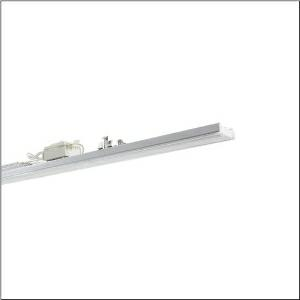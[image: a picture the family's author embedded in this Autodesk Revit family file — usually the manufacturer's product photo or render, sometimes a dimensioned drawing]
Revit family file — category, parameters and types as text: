
# Revit family: licross_r__21_recessed_mo_52te1e7n485g_828a
name_source: partatom
category: Lighting Fixtures
units: mm (PartAtom-declared; Revit-internal decimal feet)

## family parameters
Cut with Voids When Loaded = No
Host = Face
Light Source = No
Part Type = Normal
Room Calculation Point = No
Round Connector Dimension = Use Diameter
Shared = No

## types (1)
- Licross® 21 Recessed MO (1 x LED, 8530 lm, 47.9 W, 4000K)
    Apparent Load = 48 VA
    CIE Flux Codes = 85 95 99 100 100
    Color Rendering = 80
    Color Temperature = 4000K
    Default Elevation = 1800 mm
    Description = Licross® 21 Recessed MO, luminaire insert, of sheet steel, galvanised, coil coated, white, length: 1.500mm, width: 66mm, height: 67mm, LED rated luminous flux: 8.530lm, light colour: 840, control gear: ON/OFF, with plug, 3-pole, with phase selection, mains connection: 220..240V, AC, 50/60Hz, rated input power: 48W, internal wiring halogen-free, primary light control with lens, of plastic, primary optical cover: cover, of PMMA, light emission: direct distribution, primary light characteristic: symmetric, protection rating (complete): IP54, insulation class (complete): insulation class I (protective earthing), certification: CE, ENEC, VDE, UKCA, protection symbol: D if used in an environment with non-conductive dust loads with corresponding accessories, impact resistance: IK06, permissible ambient temperature for indoor applications: -35..+40°C, corresponds to IFS (International Featured Standards) requirements for safety and quality in the food industry, reducing of maximum allowable ambient temperature of 5°C with ceiling mounting, LABS conformity tested according to VDMA 24364:2018-05, packaging unit: 1 piece
    Height = 58 mm
    Lamp = 1 x LED
    Lamp Light Flux = 8530 lm
    Lamp Power = 47.9 W
    Lamp count = 1
    Length = 1500 mm
    Luminous efficacy = 178 lm/W
    Manufacturer = Siteco
    ModVariant = No
    Model = 52TE1E7N485G
    Mounting Place = Ceiling
    Mounting Type = Pendant
    Number of Poles = 1
    OnlyDefault = Yes
    Power Factor = 1
    Product Name = Licross® 21 Recessed MO
    Product group = luminaire insert | ceiling pendant
    ProductGroupID = 902
    Protection Class = Protection class I
    Protection Degree = IP 54
    RLX_Detail_Level = 1
    RLX_Emergency_Light_Flux = 0 lm
    RLX_Emergency_Type = 0
    RLX_Emergency_Type_DB = No
    RlxData = <blob elided: 21041 chars, md5=f9d62515>
    Socket = socket
    Standby Power = 0 W
    System Light Flux = 8530 lm
    System Power = 48 W
    Type Comments = Product without accessories
    Type Image = l_1296930.jpg
    URL = http://relux.com
    VarID = ---
    Voltage = 0 V
    Weight = 0.00 kg
    Width = 66 mm

## geometry (parser evidence)
native form markers: Blend x4, Sweep x11
no freeform markers — native parametric forms only
